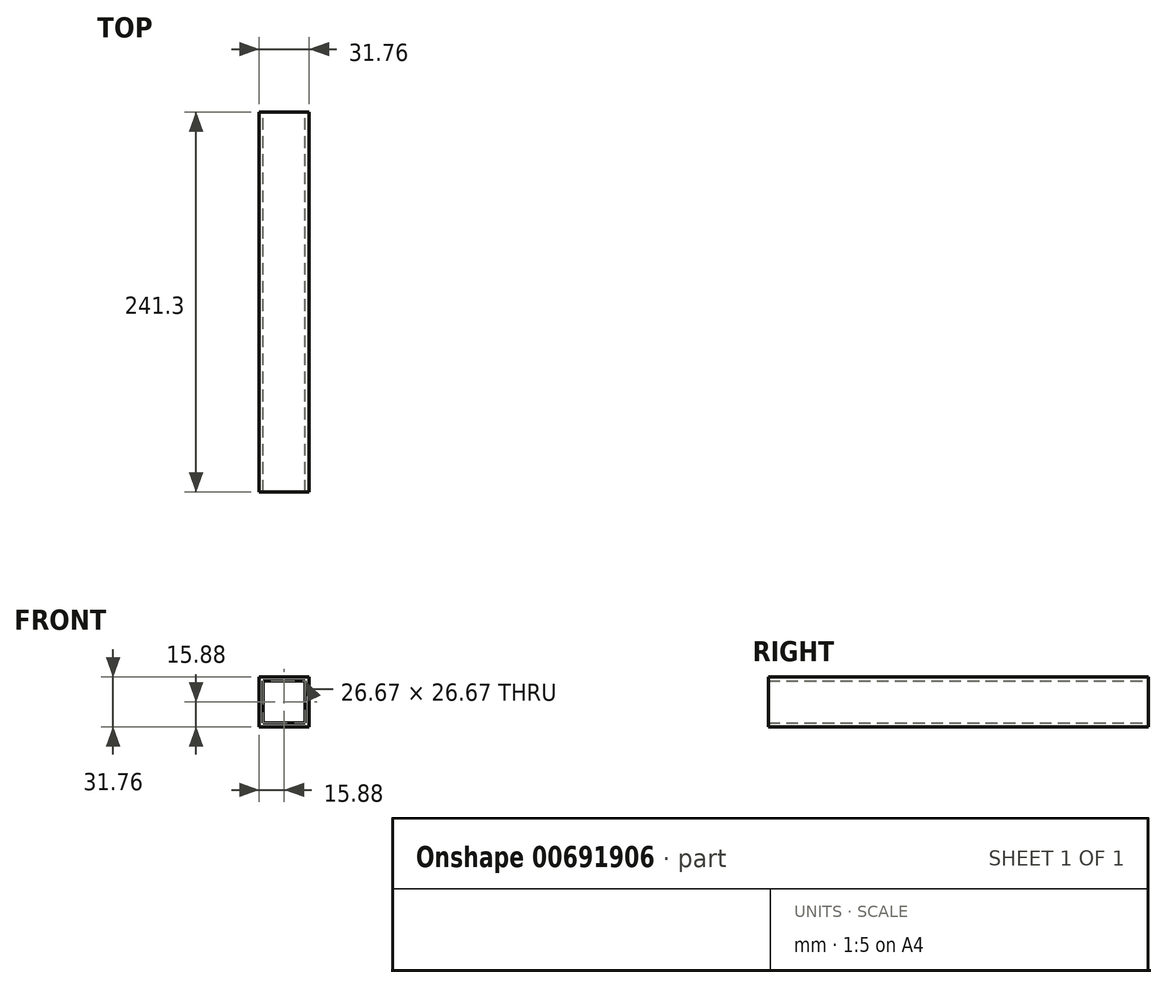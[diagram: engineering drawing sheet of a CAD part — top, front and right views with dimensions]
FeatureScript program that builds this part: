
annotation { "Feature Type Name" : "Feature", "Feature Type Description" : "" }
export const myFeature = defineFeature(function(context is Context, id is Id, definition is map)
    precondition{}
    {
        {
            var Q0;
            Q0=qCreatedBy(makeId("Front.planeOp"),FACE);
            var sketch = newSketch(context, id + "F0", { "sketchPlane" : qUnion([Q0])});
            skLineSegment(sketch, "E0.bottom", {"start": v(15.88, -15.88) * mm, "end": v(-15.88, -15.88) * mm});
            skLineSegment(sketch, "E0.top", {"start": v(15.88, 15.88) * mm, "end": v(-15.87, 15.87) * mm});
            skLineSegment(sketch, "E0.left", {"start": v(15.88, -15.88) * mm, "end": v(15.88, 15.88) * mm});
            skLineSegment(sketch, "E0.right", {"start": v(-15.88, -15.88) * mm, "end": v(-15.88, 15.88) * mm});
            skPoint(sketch, "E0.middle", {"position": v(0, 0) * mm});
            skLineSegment(sketch, "E1.bottom", {"start": v(13.33, -13.34) * mm, "end": v(-13.33, -13.34) * mm});
            skLineSegment(sketch, "E1.top", {"start": v(13.33, 13.34) * mm, "end": v(-13.33, 13.34) * mm});
            skLineSegment(sketch, "E1.left", {"start": v(13.33, -13.34) * mm, "end": v(13.33, 13.33) * mm});
            skLineSegment(sketch, "E1.right", {"start": v(-13.33, -13.34) * mm, "end": v(-13.33, 13.34) * mm});
            skSolve(sketch);
        }
        {
            var Q0;
            Q0=makeQuery(id+"F0.imprint","IMPRINT",FACE,{"disambiguationData":[TD([[makeQuery(id+"F0.imprint","IMPRINT",EDGE,{"derivedFrom":sQuery(id+"F0.wireOp",EDGE,"E0.bottom")}),-1.0]])]});
            extrude(context, id + "F1", {"entities" : qUnion([Q0]), "endBound" : BoundingType.SYMMETRIC, "depth" : 241.3 * mm, "offsetDistance" : 25.4 * mm});
        }
    });
